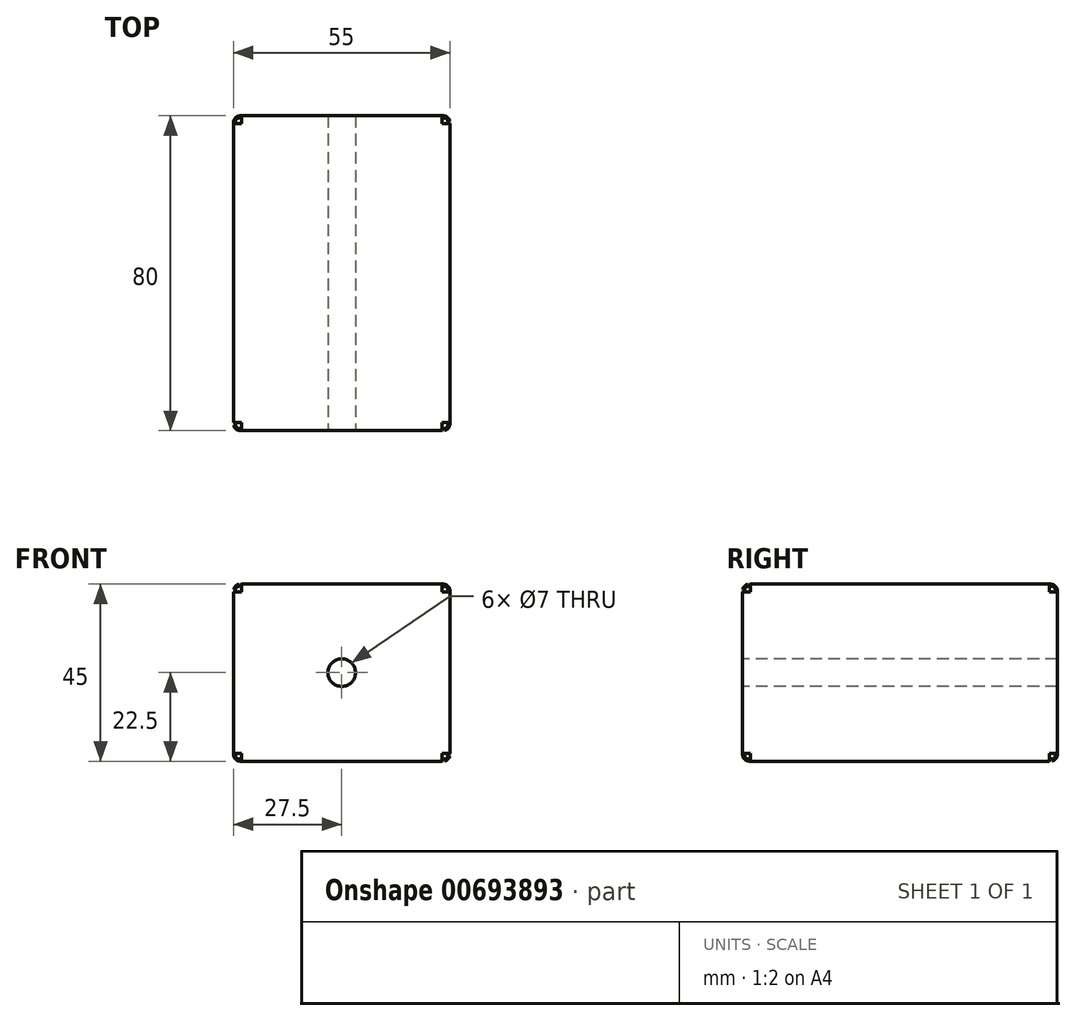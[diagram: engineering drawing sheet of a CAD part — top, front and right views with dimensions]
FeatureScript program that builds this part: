
annotation { "Feature Type Name" : "Feature", "Feature Type Description" : "" }
export const myFeature = defineFeature(function(context is Context, id is Id, definition is map)
    precondition{}
    {
        {
            var Q0;
            Q0=qCreatedBy(makeId("Front.planeOp"),FACE);
            var sketch = newSketch(context, id + "F0", { "sketchPlane" : qUnion([Q0])});
            skLineSegment(sketch, "E0.bottom", {"start": v(-27.5, 22.5) * mm, "end": v(27.5, 22.5) * mm});
            skLineSegment(sketch, "E0.top", {"start": v(-27.5, -22.5) * mm, "end": v(27.5, -22.5) * mm});
            skLineSegment(sketch, "E0.left", {"start": v(-27.5, 22.5) * mm, "end": v(-27.5, -22.5) * mm});
            skLineSegment(sketch, "E0.right", {"start": v(27.5, 22.5) * mm, "end": v(27.5, -22.5) * mm});
            skPoint(sketch, "E0.middle", {"position": v(0, 0) * mm});
            skCircle(sketch, "E1", {"center": v(0, 0) * mm, "radius": 3.5 * mm});
            skSolve(sketch);
        }
        {
            var Q0;
            Q0 = qSketchRegion(id + "F0", true);
            extrude(context, id + "F1", {"entities" : qUnion([Q0]), "oppositeDirection" : true, "depth" : 80 * mm, "offsetDistance" : 25.4 * mm});
        }
        {
            var Q0;
            Q0=makeQuery(id+"F1.opExtrude","CAP_EDGE",EDGE,{"disambiguationData":[OSD([sQuery(id+"F0.wireOp",EDGE,"E0.left")])],"isStart":true});
            var Q1;
            Q1=makeQuery(id+"F1.opExtrude","CAP_EDGE",EDGE,{"disambiguationData":[OSD([sQuery(id+"F0.wireOp",EDGE,"E0.bottom")])],"isStart":true});
            var Q2;
            Q2=makeQuery(id+"F1.opExtrude","CAP_EDGE",EDGE,{"disambiguationData":[OSD([sQuery(id+"F0.wireOp",EDGE,"E0.right")])],"isStart":true});
            var Q3;
            Q3=makeQuery(id+"F1.opExtrude","CAP_EDGE",EDGE,{"disambiguationData":[OSD([sQuery(id+"F0.wireOp",EDGE,"E0.top")])],"isStart":true});
            var Q4;
            Q4=makeQuery(id+"F1.opExtrude","SWEPT_EDGE",EDGE,{"disambiguationData":[OSD([sQuery(id+"F0.wireOp",EDGE,"E0.bottom"),sQuery(id+"F0.wireOp",EDGE,"E0.left")])]});
            var Q5;
            Q5=makeQuery(id+"F1.opExtrude","SWEPT_EDGE",EDGE,{"disambiguationData":[OSD([sQuery(id+"F0.wireOp",EDGE,"E0.top"),sQuery(id+"F0.wireOp",EDGE,"E0.left")])]});
            var Q6;
            Q6=makeQuery(id+"F1.opExtrude","CAP_EDGE",EDGE,{"disambiguationData":[OSD([sQuery(id+"F0.wireOp",EDGE,"E0.left")])],"isStart":false});
            var Q7;
            Q7=makeQuery(id+"F1.opExtrude","CAP_EDGE",EDGE,{"disambiguationData":[OSD([sQuery(id+"F0.wireOp",EDGE,"E0.bottom")])],"isStart":false});
            var Q8;
            Q8=makeQuery(id+"F1.opExtrude","SWEPT_EDGE",EDGE,{"disambiguationData":[OSD([sQuery(id+"F0.wireOp",EDGE,"E0.bottom"),sQuery(id+"F0.wireOp",EDGE,"E0.right")])]});
            var Q9;
            Q9=makeQuery(id+"F1.opExtrude","CAP_EDGE",EDGE,{"disambiguationData":[OSD([sQuery(id+"F0.wireOp",EDGE,"E0.right")])],"isStart":false});
            var Q10;
            Q10=makeQuery(id+"F1.opExtrude","SWEPT_EDGE",EDGE,{"disambiguationData":[OSD([sQuery(id+"F0.wireOp",EDGE,"E0.top"),sQuery(id+"F0.wireOp",EDGE,"E0.right")])]});
            var Q11;
            Q11=makeQuery(id+"F1.opExtrude","CAP_EDGE",EDGE,{"disambiguationData":[OSD([sQuery(id+"F0.wireOp",EDGE,"E0.top")])],"isStart":false});
            fillet(context, id + "F2", {"entities" : qUnion([Q0, Q1, Q2, Q3, Q4, Q5, Q6, Q7, Q8, Q9, Q10, Q11]), "radius" : 2 * mm, "tangentPropagation" : true, "rho" : 0.5, "crossSection" : FilletCrossSection.CONIC, "allowEdgeOverflow" : false});
        }
    });
